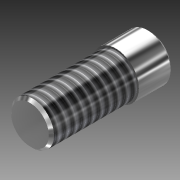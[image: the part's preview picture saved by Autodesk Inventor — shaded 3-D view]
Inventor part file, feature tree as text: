
AUTODESK INVENTOR PART (.ipt)
format: ipt  version: 2013 (Build 170138000, 138)  size: 108,544 bytes
history: native  units: mm (DEFAULTED — no unit token found)
features: extrude x2, chamfer x2, sketch x2, thread x1, reference x1
ambient origin geometry x8: Origin, YZ Plane, XZ Plane, XY Plane, X Axis, Y Axis, Z Axis, Center Point
bodies: Solid1 (feature_tree)
feature tree (8):
  extrude  "Extrusion1"  Depth=5.08mm TaperAngle=0.0deg
  chamfer  "Chamfer1"  Distance=0.381mm
  extrude  "Extrusion2"  Depth=12.7mm TaperAngle=0.0deg
  chamfer  "Chamfer2"  Distance=0.381mm
  thread  "Thread1"  [1 undecoded]
  sketch  "Sketch1"  dims[d0=6.858mm d1=5.08mm d2=0.0mm d3=0.381mm d4=3.175mm]
  reference  "Reference1"
  sketch  "Sketch2"  dims[d5=6.35mm d6=12.7mm d7=0.0mm d8=0.381mm d9=3.175mm d10=25.4mm d11=0.0mm d12=45.0deg d13=45.0deg]
note: 1 required parameter value undecoded (feature->parameter linkage not recoverable at this tier; creation-order binding heuristic only, values carry confidence <= 0.55)
